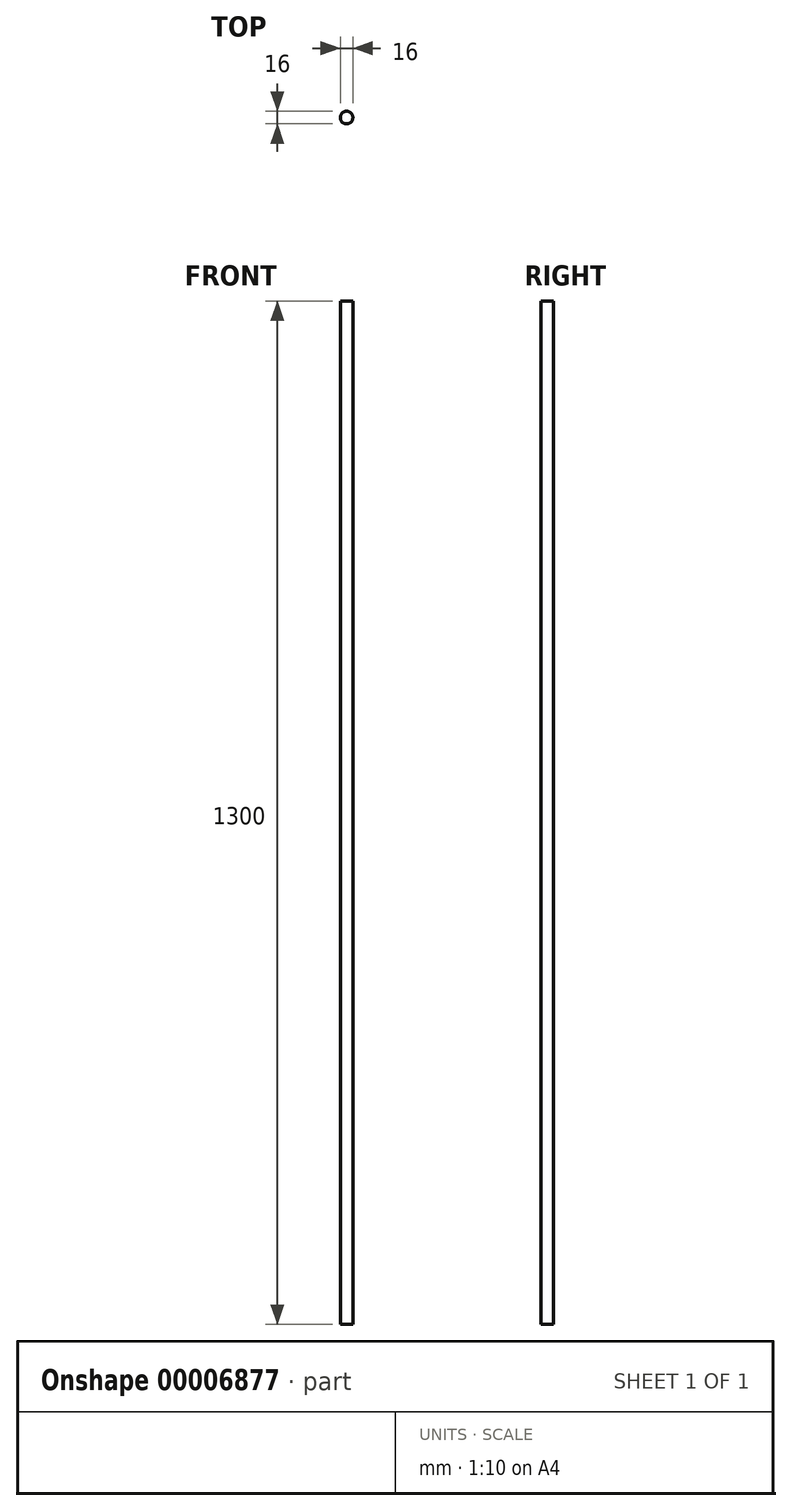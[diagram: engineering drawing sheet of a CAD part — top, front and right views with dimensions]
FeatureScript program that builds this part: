
annotation { "Feature Type Name" : "Feature", "Feature Type Description" : "" }
export const myFeature = defineFeature(function(context is Context, id is Id, definition is map)
    precondition{}
    {
        {
            var Q0;
            Q0=qCreatedBy(makeId("Top.planeOp"),FACE);
            var sketch = newSketch(context, id + "F0", { "sketchPlane" : qUnion([Q0])});
            skCircle(sketch, "E0", {"center": v(0, 0) * mm, "radius": 8 * mm});
            skSolve(sketch);
        }
        {
            var Q0;
            Q0=qSketchRegion(id+"F0",true);
            extrude(context, id + "F1", {"entities" : qUnion([Q0]), "depth" : (1300) * mm});
        }
    });
